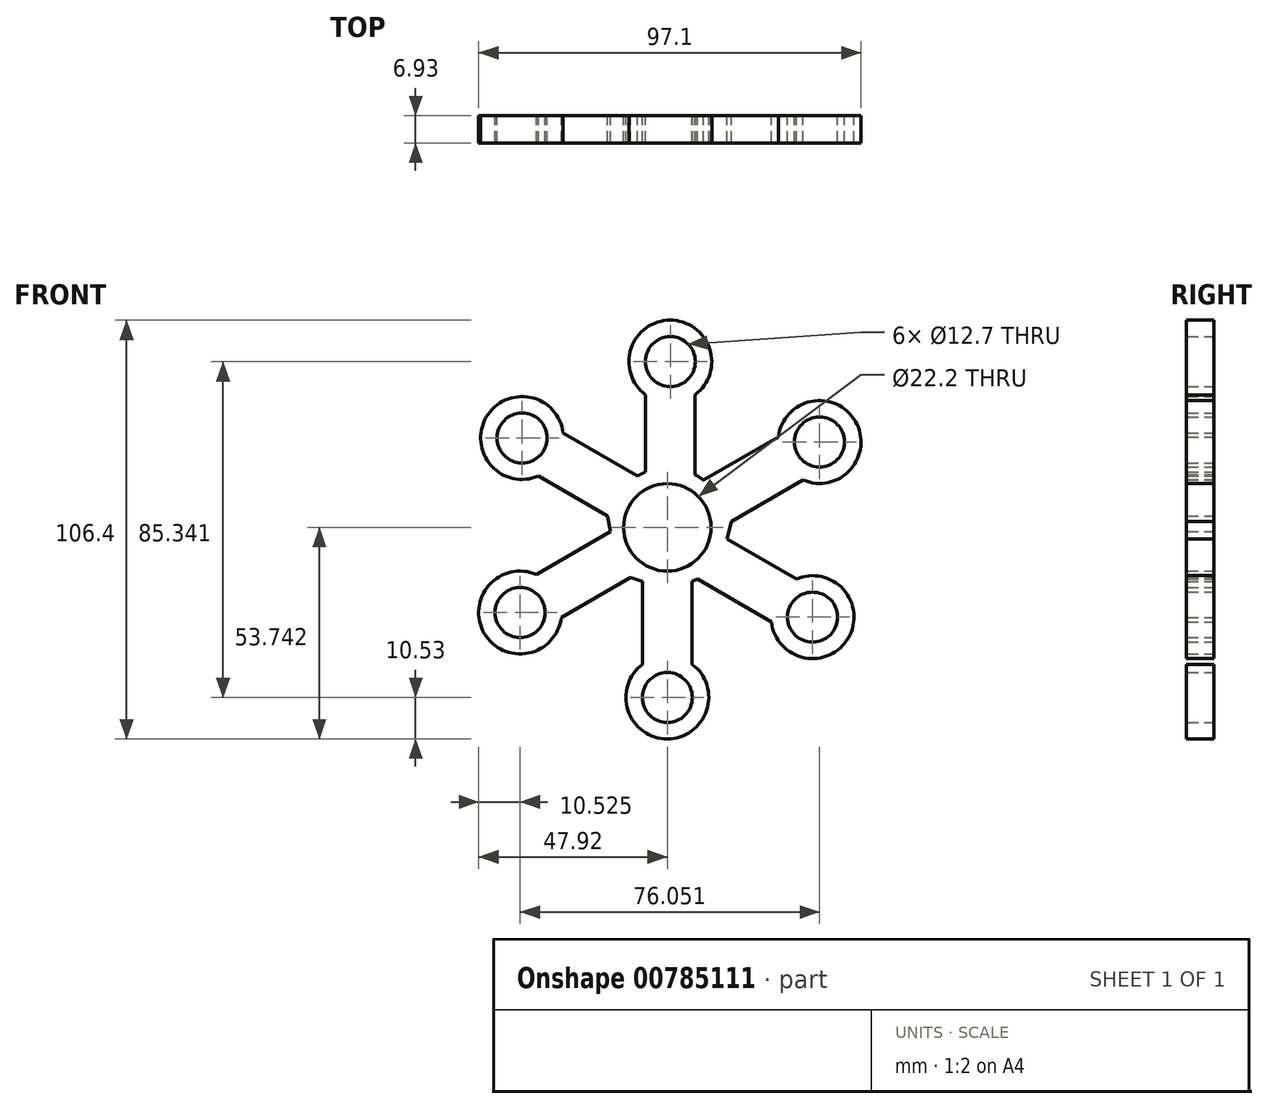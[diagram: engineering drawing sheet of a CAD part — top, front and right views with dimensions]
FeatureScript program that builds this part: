
annotation { "Feature Type Name" : "Feature", "Feature Type Description" : "" }
export const myFeature = defineFeature(function(context is Context, id is Id, definition is map)
    precondition{}
    {
        {
            var Q0;
            Q0=qCreatedBy(makeId("Front.planeOp"),FACE);
            var sketch = newSketch(context, id + "F0", { "sketchPlane" : qUnion([Q0])});
            skCircle(sketch, "E0", {"center": v(0, 0.03) * mm, "radius": 11.1 * mm});
            skCircle(sketch, "E1", {"center": v(0, -43.18) * mm, "radius": 6.35 * mm});
            skLineSegment(sketch, "E2", {"start": v(0, 0) * mm, "end": v(0, -11.07) * mm, "construction": true});
            skLineSegment(sketch, "E3", {"start": v(6.3, -43.92) * mm, "end": v(6.3, -42.44) * mm});
            skLineSegment(sketch, "E4", {"start": v(-6.3, -43.92) * mm, "end": v(-6.3, -42.44) * mm});
            skCircle(sketch, "E5.1.0", {"center": v(38.66, 21.74) * mm, "radius": 6.35 * mm});
            skLineSegment(sketch, "E5.1.1", {"start": v(36.14, 27.57) * mm, "end": v(34.86, 26.83) * mm});
            skLineSegment(sketch, "E5.1.2", {"start": v(42.45, 16.65) * mm, "end": v(41.17, 15.9) * mm});
            skCircle(sketch, "E5.2.0", {"center": v(-36.9, 22.76) * mm, "radius": 6.35 * mm});
            skLineSegment(sketch, "E5.2.1", {"start": v(-40.69, 17.66) * mm, "end": v(-39.4, 16.92) * mm});
            skLineSegment(sketch, "E5.2.2", {"start": v(-34.38, 28.59) * mm, "end": v(-33.1, 27.85) * mm});
            skPoint(sketch, "E5.center", {"position": v(0.59, 0.44) * mm});
            skArc(sketch, "E6", {"start": v(9.23, 12.03) * mm, "mid": v(8.18, 12.77) * mm, "end": v(7.07, 13.42) * mm});
            skLineSegment(sketch, "E7.trimOffspring", {"start": v(-4.23, 11.18) * mm, "end": v(-3.28, 10.63) * mm});
            skLineSegment(sketch, "E8.trimOffspring", {"start": v(-11.09, 0.57) * mm, "end": v(-10.53, 0.26) * mm});
            skPoint(sketch, "E9.orphan", {"position": v(-6.3, -9.1) * mm});
            skPoint(sketch, "E10.orphan", {"position": v(6.3, -9.1) * mm});
            skLineSegment(sketch, "E11.trimOffspring", {"start": v(12.3, -0.76) * mm, "end": v(11, -1.52) * mm});
            skLineSegment(sketch, "E12.trimOffspring", {"start": v(6, 10.16) * mm, "end": v(5.32, 9.77) * mm});
            skLineSegment(sketch, "E13.trimOffspring", {"start": v(0, -36.83) * mm, "end": v(0, -49.53) * mm, "construction": true});
            skArc(sketch, "E14", {"start": v(-26.44, 24) * mm, "mid": v(-46.01, 28.02) * mm, "end": v(-32.74, 13.08) * mm});
            skArc(sketch, "E15", {"start": v(34.5, 12.06) * mm, "mid": v(47.77, 27) * mm, "end": v(28.2, 22.98) * mm});
            skArc(sketch, "E16", {"start": v(-6.3, -34.75) * mm, "mid": v(0, -53.7) * mm, "end": v(6.3, -34.75) * mm});
            skLineSegment(sketch, "E17.2.0", {"start": v(34.38, -28.59) * mm, "end": v(33.1, -27.85) * mm});
            skLineSegment(sketch, "E17.2.1", {"start": v(40.69, -17.66) * mm, "end": v(39.4, -16.92) * mm});
            skArc(sketch, "E17.2.2", {"start": v(26.44, -24) * mm, "mid": v(46.01, -28.02) * mm, "end": v(32.74, -13.08) * mm});
            skCircle(sketch, "E17.2.3", {"center": v(36.9, -22.76) * mm, "radius": 6.35 * mm});
            skPoint(sketch, "E17.center", {"position": v(0, 0) * mm});
            skLineSegment(sketch, "E17.anchor1", {"start": v(0, 0) * mm, "end": v(-8.55, 7.1) * mm, "construction": true});
            skLineSegment(sketch, "E17.anchor2", {"start": v(0, 0) * mm, "end": v(8.52, -7.08) * mm, "construction": true});
            skLineSegment(sketch, "E18.1.0", {"start": v(7.07, 42.9) * mm, "end": v(7.07, 41.42) * mm});
            skLineSegment(sketch, "E18.1.1", {"start": v(-5.55, 42.9) * mm, "end": v(-5.55, 41.42) * mm});
            skCircle(sketch, "E18.1.2", {"center": v(0.76, 42.16) * mm, "radius": 6.35 * mm});
            skArc(sketch, "E18.1.3", {"start": v(7.07, 33.73) * mm, "mid": v(0.76, 52.69) * mm, "end": v(-5.55, 33.73) * mm});
            skLineSegment(sketch, "E18.2.0", {"start": v(-41.19, -16.5) * mm, "end": v(-39.9, -15.76) * mm});
            skLineSegment(sketch, "E18.2.1", {"start": v(-34.88, -27.42) * mm, "end": v(-33.6, -26.68) * mm});
            skCircle(sketch, "E18.2.2", {"center": v(-37.4, -21.59) * mm, "radius": 6.35 * mm});
            skArc(sketch, "E18.2.3", {"start": v(-33.25, -11.91) * mm, "mid": v(-46.51, -26.85) * mm, "end": v(-26.94, -22.84) * mm});
            skPoint(sketch, "E18.center", {"position": v(0.09, -0.73) * mm});
            skArc(sketch, "E19.trimOffspring", {"start": v(-5.55, 14.12) * mm, "mid": v(-6.6, 13.66) * mm, "end": v(-7.6, 13.13) * mm});
            skLineSegment(sketch, "E20.trimOffspring", {"start": v(-31.62, 26.3) * mm, "end": v(-34.38, 28.59) * mm, "construction": true});
            skLineSegment(sketch, "E21.trimOffspring", {"start": v(31.62, -26.3) * mm, "end": v(34.38, -28.59) * mm, "construction": true});
            skLineSegment(sketch, "E22.trimOffspring", {"start": v(-6.3, -34.75) * mm, "end": v(-6.3, -13.73) * mm});
            skLineSegment(sketch, "E23.trimOffspring", {"start": v(6.3, -34.75) * mm, "end": v(6.3, -13.73) * mm});
            skLineSegment(sketch, "E24.trimOffspring", {"start": v(-26.94, -22.84) * mm, "end": v(-9.38, -12.7) * mm});
            skLineSegment(sketch, "E25.trimOffspring", {"start": v(-33.25, -11.91) * mm, "end": v(-14.4, -1.04) * mm});
            skLineSegment(sketch, "E26.trimOffspring", {"start": v(-32.74, 13.08) * mm, "end": v(-15.18, 2.94) * mm});
            skLineSegment(sketch, "E27.trimOffspring", {"start": v(-26.44, 24) * mm, "end": v(-7.6, 13.13) * mm});
            skLineSegment(sketch, "E28.trimOffspring", {"start": v(7.07, 33.73) * mm, "end": v(7.07, 11.98) * mm});
            skLineSegment(sketch, "E29.trimOffspring", {"start": v(-5.55, 33.73) * mm, "end": v(-5.55, 13.45) * mm});
            skLineSegment(sketch, "E30.trimOffspring", {"start": v(34.5, 12.06) * mm, "end": v(16.33, 1.57) * mm});
            skLineSegment(sketch, "E31.trimOffspring", {"start": v(28.2, 22.98) * mm, "end": v(9.23, 12.03) * mm});
            skLineSegment(sketch, "E32.trimOffspring", {"start": v(32.74, -13.08) * mm, "end": v(15.18, -2.94) * mm});
            skLineSegment(sketch, "E33.trimOffspring", {"start": v(26.44, -24) * mm, "end": v(7.6, -13.13) * mm});
            skLineSegment(sketch, "E34", {"start": v(-14.4, -1.04) * mm, "end": v(-15.18, 2.94) * mm});
            skLineSegment(sketch, "E35", {"start": v(-6.3, -13.73) * mm, "end": v(-9.38, -12.7) * mm});
            skLineSegment(sketch, "E36", {"start": v(15.18, -2.94) * mm, "end": v(16.33, 1.57) * mm});
            skLineSegment(sketch, "E37", {"start": v(6.3, -13.73) * mm, "end": v(7.6, -13.13) * mm});
            skSolve(sketch);
        }
        {
            var Q0;
            {var subQ30=sQuery(id+"F0.wireOp",EDGE,"E6");Q0=makeQuery(id+"F0.imprint","IMPRINT",FACE,{"disambiguationData":[TD([[makeQuery(id+"F0.imprint","IMPRINT",EDGE,{"derivedFrom":subQ30}),1.0]])]});}
            extrude(context, id + "F1", {"entities" : qUnion([Q0]), "depth" : 6.93 * mm, "offsetDistance" : 25.4 * mm});
        }
    });
